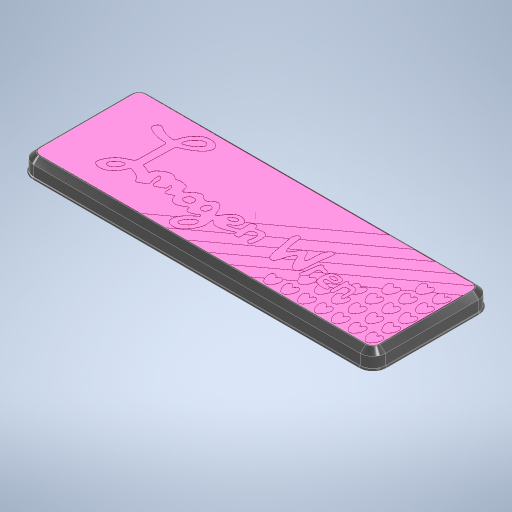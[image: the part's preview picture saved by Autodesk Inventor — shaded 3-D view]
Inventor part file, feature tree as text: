
AUTODESK INVENTOR PART (.ipt)
format: ipt  version: 2024.1 (Build 281209000, 209)  size: 2,141,184 bytes
history: native  units: mm
features: projected_geometry x29, extrude x20, fillet x11, chamfer x5, other x4, pattern_circular x2, sketch x2, plane x1, pattern_linear x1, mirror x1
ambient origin geometry x8: Origin, YZ Plane, XZ Plane, XY Plane, X Axis, Y Axis, Z Axis, Center Point
bodies: Body1 (feature_tree), Body2 (feature_tree), Body3 (feature_tree)
feature tree (76):
  other  "case"
  extrude  "Extrusion1"  Depth=56.0mm
  extrude  "Extrusion2"  Depth=28.0mm
  extrude  "Extrusion3"  Depth=18.0mm TaperAngle=0.0deg
  fillet  "Fillet1"  Radius=2.0mm
  fillet  "Fillet2"  Radius=4.0mm
  fillet  "Fillet3"  Radius=20.0mm
  pattern_circular  "Circular Pattern1"  [2 undecoded]
  fillet  "Fillet4"  Radius=20.0mm
  chamfer  "Chamfer1"  Distance=96.0mm
  extrude  "Extrusion4"  Depth=65.0mm
  chamfer  "Chamfer2"  Distance=74.2mm
  extrude  "Extrusion5"  Depth=12.0mm
  pattern_circular  "Circular Pattern2"  [2 undecoded]
  fillet  "Fillet5"  Radius=12.4mm
  fillet  "Fillet6"  Radius=0.95mm
  fillet  "Fillet10"  Radius=0.95mm
  fillet  "Fillet11"  Radius=2.0mm
  fillet  "Fillet12"  Radius=3.7mm
  extrude  "Extrusion6"  Depth=17.6mm TaperAngle=0.0deg
  plane  "Work Plane1"
  extrude  "Extrusion7"  Depth=25.0mm
  extrude  "Extrusion8"  Depth=16.6mm
  extrude  "Extrusion9"  Depth=4.0mm
  fillet  "Fillet8"  Radius=3.0mm
  extrude  "Extrusion10"  Depth=4.0mm
  pattern_linear  "Rectangular Pattern1"  Count1=2 Spacing1=180.0deg
  mirror  "Mirror1"
  extrude  "Extrusion11"  Depth=6.0mm
  extrude  "Extrusion15"  Depth=6.0mm TaperAngle=45.0deg
  extrude  "Extrusion16"  Depth=1.3mm
  chamfer  "Chamfer4"  Distance=5.0mm
  extrude  "Extrusion18"  Depth=3.0mm TaperAngle=45.0deg
  extrude  "Extrusion19"  Depth=6.0mm
  extrude  "Extrusion12"  Depth=6.5mm
  extrude  "Extrusion13"  Depth=6.5mm
  extrude  "Extrusion14"  Depth=22.0mm
  extrude  "Extrusion17"  Depth=2.0mm TaperAngle=0.0deg
  chamfer  "Chamfer5"  Distance=20.0mm Angle=360.0deg
  chamfer  "Chamfer6"  Distance=6.5mm
  extrude  "Extrusion20"  Depth=6.5mm
  fillet  "Fillet13"  Radius=2.0mm
  projected_geometry  "Projected Loop1"
  projected_geometry  "Projected Loop5"
  other  "Work Axis1"
  projected_geometry  "Projected Loop7"
  other  "lid"
  projected_geometry  "Projected Loop8"
  projected_geometry  "Projected Loop9"
  projected_geometry  "Projected Loop10"
  projected_geometry  "Projected Loop11"
  sketch  "Sketch15"  dims[d0=167.0mm d1=56.0mm]
  sketch  "Sketch16"  dims[d2=83.5mm d3=28.0mm d4=18.0mm d5=0.0mm d6=2.0mm d8=4.0mm d9=20.0mm d10=4.0mm d11=20.0mm d12=96.0mm d13=65.0mm d14=74.2mm d15=12.0mm d16=14.3mm d17=12.4mm d18=0.95mm d19=0.95mm d20=2.0mm d21=3.7mm d22=17.6mm d23=0.0mm d24=25.0mm d27=16.6mm d28=-1.745329mm d29=4.0mm d30=3.0mm d31=4.0mm d32=20.0mm d33=180.0deg d35=6.0mm d36=6.0mm d37=2.0mm d38=45.0deg d39=1.3mm d40=5.0mm d41=0.0mm d42=3.0mm d43=2.0mm d44=45.0deg d45=6.0mm d46=6.5mm d47=6.5mm d48=22.0mm d49=2.0mm d50=0.0mm d51=20.0mm d52=360.0deg d54=6.5mm d55=6.5mm d56=2.0mm d57=3.0mm d59=6.5mm d60=6.45mm d61=1.0mm d62=3.0mm d63=0.0mm d64=3.1mm d65=0.0mm d69=1.8mm d70=0.0mm d71=0.5mm d72=1.0mm d73=0.0mm d74=0.5mm d75=60.0mm d76=20.0mm d77=29.0mm d79=8.5mm d80=-1.745329mm d82=70.0mm d84=124.0mm d85=55.0mm d86=1.0mm d89=0.06mm d90=0.0mm d91=0.02mm d92=0.0mm d93=30.0deg d94=1.0mm d95=6.0mm d96=6.0mm d97=7.0mm d98=6.0mm d99=6.0mm d101=1.0mm d108=3.0mm d109=3.0mm d110=0.04mm d111=0.0mm d112=1.6mm d113=1.6mm d114=1.1mm d115=1.1mm d116=7.0mm d117=3.0mm d119=2.0mm d120=1.1mm d121=1.1mm d122=1.5mm d123=1.5mm d124=1.5mm d125=1.0mm d126=1.1mm d127=1.1mm d128=1.8mm d131=2.0mm d132=1.5mm d133=1.5mm d140=50.0mm d142=8.0mm d143=60.0mm d145=8.0mm d148=0.0mm d149=0.0mm d150=0.0mm d151=0.0mm d152=3.5mm d153=0.0mm d154=2.5mm d155=2.0mm d156=45.0deg d158=0.4mm d159=0.4mm d160=0.0mm d163=3.0mm d164=1.5mm d165=0.4mm d166=0.0mm d167=3.1mm d168=0.0mm d169=1.5mm d170=2.0mm d171=45.0deg d172=1.5mm d173=2.0mm d174=45.0deg d175=8.0mm d176=8.0mm d177=45.0mm d178=16.0mm d179=3.0mm d180=3.0mm d181=3.0mm d182=0.0mm d183=0.0mm d184=1.0mm]
  other  "lid-part2"
  projected_geometry  "Projected Loop12"
  projected_geometry  "Projected Loop13"
  projected_geometry  "Projected Loop14"
  projected_geometry  "Projected Loop15"
  projected_geometry  "Projected Loop16"
  projected_geometry  "Projected Loop17"
  projected_geometry  "Projected Loop18"
  projected_geometry  "Projected Loop19"
  projected_geometry  "Projected Loop20"
  projected_geometry  "Projected Loop21"
  projected_geometry  "Projected Loop22"
  projected_geometry  "Projected Loop23"
  projected_geometry  "Projected Loop24"
  projected_geometry  "Projected Loop25"
  projected_geometry  "Projected Loop26"
  projected_geometry  "Projected Loop27"
  projected_geometry  "Projected Loop28"
  projected_geometry  "Projected Loop29"
  projected_geometry  "Projected Loop30"
  projected_geometry  "Projected Loop31"
  projected_geometry  "Projected Loop32"
  projected_geometry  "Projected Loop33"
note: 4 required parameter values undecoded (feature->parameter linkage not recoverable at this tier; creation-order binding heuristic only, values carry confidence <= 0.55)
